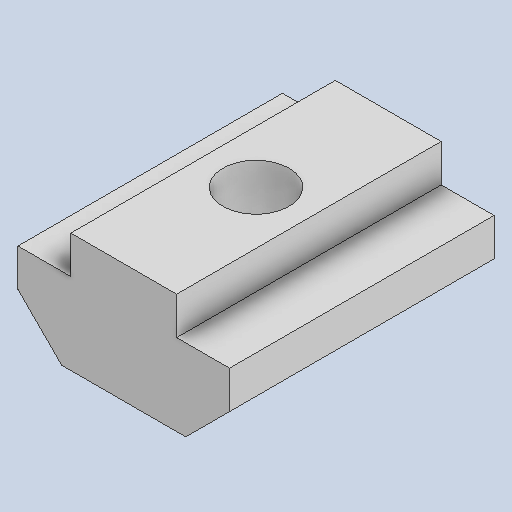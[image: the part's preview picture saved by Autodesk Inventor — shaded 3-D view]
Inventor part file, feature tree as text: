
AUTODESK INVENTOR PART (.ipt)
format: ipt  version: 2022 (Build 260153000, 153)  size: 99,328 bytes
history: native  units: in
note: dims shown in document units (in); Inventor stores cm internally (conversion verified against a paired STEP export)
features: hole x1
ambient origin geometry x8: Origin, YZ Plane, XZ Plane, XY Plane, X Axis, Y Axis, Z Axis, Center Point
bodies: Solid1 (feature_tree)
feature tree (1):
  hole  "Hole2"  [1 undecoded]
note: 1 required parameter value undecoded (feature->parameter linkage not recoverable at this tier; creation-order binding heuristic only, values carry confidence <= 0.55)
